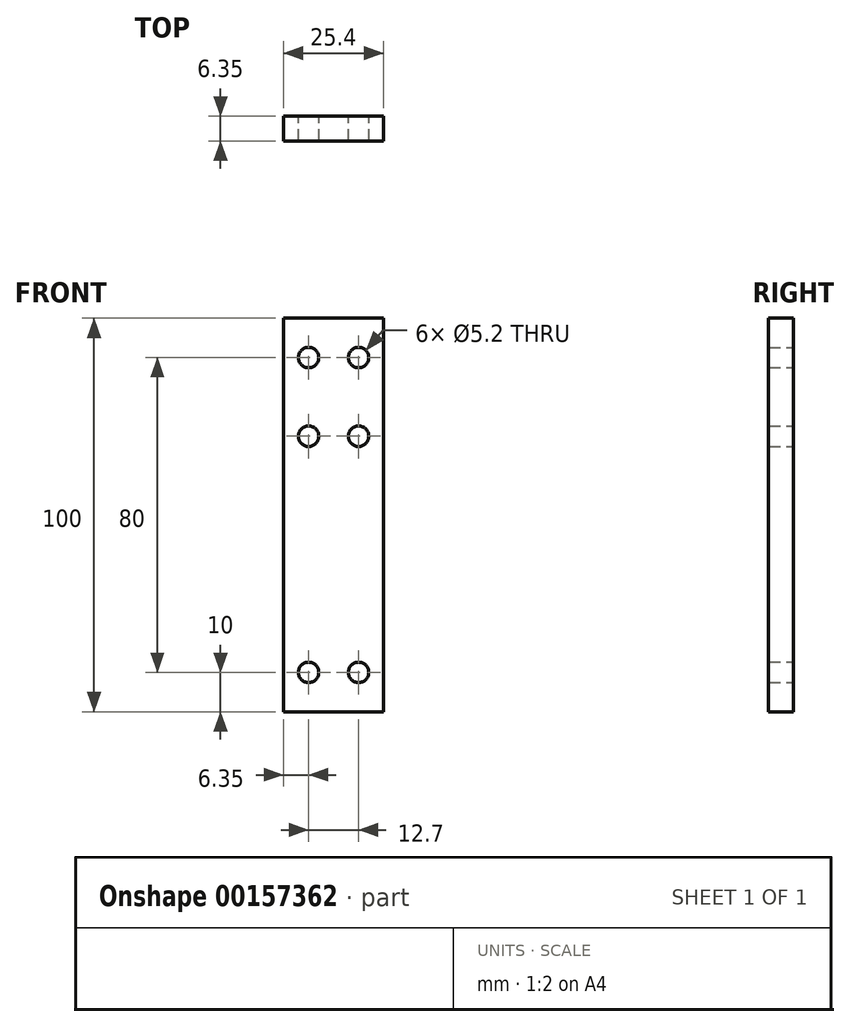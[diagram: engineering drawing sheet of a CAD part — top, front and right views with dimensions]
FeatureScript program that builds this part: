
annotation { "Feature Type Name" : "Feature", "Feature Type Description" : "" }
export const myFeature = defineFeature(function(context is Context, id is Id, definition is map)
    precondition{}
    {
        {
            var Q0;
            Q0=qCreatedBy(makeId("Front.planeOp"),FACE);
            var sketch = newSketch(context, id + "F0", { "sketchPlane" : qUnion([Q0])});
            skLineSegment(sketch, "E0.bottom", {"start": v(12.7, 50) * mm, "end": v(-12.7, 50) * mm});
            skLineSegment(sketch, "E0.top", {"start": v(12.7, -50) * mm, "end": v(-12.7, -50) * mm});
            skLineSegment(sketch, "E0.left", {"start": v(12.7, 50) * mm, "end": v(12.7, -50) * mm});
            skLineSegment(sketch, "E0.right", {"start": v(-12.7, 50) * mm, "end": v(-12.7, -50) * mm});
            skPoint(sketch, "E0.middle", {"position": v(0, 0) * mm});
            skLineSegment(sketch, "E1", {"start": v(0, 0) * mm, "end": v(0, 36.45) * mm, "construction": true});
            skCircle(sketch, "E2", {"center": v(-6.35, 40) * mm, "radius": 2.6 * mm});
            skCircle(sketch, "E3", {"center": v(-6.35, 20) * mm, "radius": 2.6 * mm});
            skCircle(sketch, "E4", {"center": v(-6.35, -40) * mm, "radius": 2.6 * mm});
            skLineSegment(sketch, "E5", {"start": v(0, 20) * mm, "end": v(-12.7, 20) * mm, "construction": true});
            skCircle(sketch, "E6.MirrorC", {"center": v(6.35, -40) * mm, "radius": 2.6 * mm});
            skCircle(sketch, "E7.MirrorC", {"center": v(6.35, 20) * mm, "radius": 2.6 * mm});
            skCircle(sketch, "E8.MirrorC", {"center": v(6.35, 40) * mm, "radius": 2.6 * mm});
            skSolve(sketch);
        }
        {
            var Q0;
            Q0=makeQuery(id+"F0.imprint","IMPRINT",FACE,{"disambiguationData":[TD([[makeQuery(id+"F0.imprint","IMPRINT",EDGE,{"derivedFrom":sQuery(id+"F0.wireOp",EDGE,"E0.bottom")}),1.0]])]});
            extrude(context, id + "F1", {"entities" : qUnion([Q0]), "depth" : 6.35 * mm});
        }
    });
